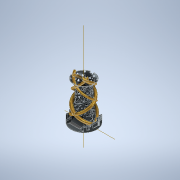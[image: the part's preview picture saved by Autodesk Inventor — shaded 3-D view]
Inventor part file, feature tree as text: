
AUTODESK INVENTOR PART (.ipt)
format: ipt  version: 2022 (Build 260153000, 153)  size: 7,433,728 bytes
history: native  units: mm
features: sketch x27, extrude x26, helix x5, plane x4, fillet x3, revolve x2, pattern_circular x2, chamfer x2
ambient origin geometry x8: Origin, YZ Plane, XZ Plane, XY Plane, X Axis, Y Axis, Z Axis, Center Point
bodies: Solid1 (feature_tree)
feature tree (71):
  revolve  "Revolution1"  [1 undecoded]
  plane  "Work Plane1"
  extrude  "Extrusion4"  Depth=20.0mm
  extrude  "Extrusion2"  Depth=19.0mm
  pattern_circular  "Circular Pattern2"  Count=9  [1 undecoded]
  plane  "Work Plane3"
  extrude  "Extrusion3"  Depth=10.0mm
  pattern_circular  "Circular Pattern3"  Count=7  [1 undecoded]
  helix  "Coil1"  [1 undecoded]
  helix  "Coil2"  [1 undecoded]
  helix  "Coil3"  [1 undecoded]
  helix  "Coil4"  [1 undecoded]
  helix  "Coil5"  [1 undecoded]
  extrude  "Extrusion5"  Depth=20.0mm
  revolve  "Revolution2"  [1 undecoded]
  extrude  "Extrusion6"  Depth=30.0mm
  extrude  "Extrusion15"  Depth=15.0mm
  extrude  "Extrusion16"  Depth=30.0mm
  extrude  "Extrusion17"  Depth=13.0mm
  extrude  "Extrusion18"  Depth=39.0mm
  extrude  "Extrusion19"  Depth=11.0mm
  extrude  "Extrusion20"  Depth=10.0mm
  extrude  "Extrusion21"  Depth=11.0mm
  extrude  "Extrusion22"  Depth=9.0mm
  extrude  "Extrusion23"  Depth=3.0mm TaperAngle=0.0deg
  extrude  "Extrusion25"  Depth=54.0mm TaperAngle=0.0deg
  extrude  "Extrusion26"  Depth=35.0mm
  extrude  "Extrusion27"  Depth=30.0mm
  extrude  "Extrusion28"  Depth=35.0mm
  extrude  "Extrusion29"  Depth=35.0mm
  extrude  "Extrusion30"  Depth=5.0mm
  extrude  "Extrusion31"  Depth=10.0mm TaperAngle=0.0deg
  plane  "Work Plane4"
  extrude  "Extrusion32"  Depth=5.0mm TaperAngle=0.0deg
  extrude  "Extrusion33"  Depth=10.0mm TaperAngle=0.0deg
  chamfer  "Chamfer2"  Distance=15.0mm
  chamfer  "Chamfer3"  Distance=0.2mm
  fillet  "Fillet5"  Radius=5.0mm
  fillet  "Fillet6"  Radius=10.0mm
  extrude  "Extrusion34"  Depth=15.0mm TaperAngle=0.0deg
  fillet  "Fillet16"  Radius=3.0mm
  extrude  "Extrusion35"  Depth=1.0mm TaperAngle=0.0deg
  extrude  "Extrusion36"  Depth=10.0mm TaperAngle=0.0deg
  sketch  "Sketch1"  dims[d11=50.0mm d12=40.0mm]
  sketch  "Sketch3"  dims[d13=20.0mm d14=20.0mm]
  plane  "Work Plane2"
  sketch  "Sketch4"  dims[d15=23.0mm d16=19.0mm d17=90.0mm]
  sketch  "Sketch5"  dims[d18=32.0mm d19=10.0mm]
  sketch  "Sketch7"  dims[d20=151.0mm]
  sketch  "Sketch8"  dims[d26=2.0mm]
  sketch  "Sketch9"  dims[d27=2.0mm]
  sketch  "Sketch10"  dims[d28=2.0mm]
  sketch  "Sketch11"  dims[d29=2.0mm]
  sketch  "Sketch13"  dims[d30=2.0mm]
  sketch  "Sketch16"  dims[d31=90.0deg d32=70.0mm d38=77.75mm d39=0.0mm d40=40.0mm d41=360.0deg d43=70.0mm d44=77.75mm d45=0.0mm d46=40.0mm d47=360.0deg]
  sketch  "Sketch17"  dims[d49=20.0mm d50=20.0mm]
  sketch  "Sketch20"  dims[d51=20.0mm d52=20.0mm]
  sketch  "Sketch21"  dims[d53=40.0mm d54=30.0mm]
  sketch  "Sketch22"  dims[d55=30.0mm d56=15.0mm]
  sketch  "Sketch26"  dims[d57=15.0mm d58=30.0mm]
  sketch  "Sketch27"  dims[d59=77.75mm d60=0.0mm]
  sketch  "Sketch28"  dims[d63=70.0mm d64=100.0mm d65=10.0mm d66=-0.567232mm d67=90.0deg d68=90.0deg d69=90.0deg d70=90.0deg d71=13.0mm]
  sketch  "Sketch30"  dims[d72=10.0mm d73=39.0mm]
  sketch  "Sketch31"  dims[d74=140.0mm d75=160.0mm d76=10.0mm d77=-0.645772mm d78=90.0deg d79=90.0deg d80=90.0deg d81=90.0deg d82=11.0mm]
  sketch  "Sketch33"  dims[d83=39.0mm d84=10.0mm]
  sketch  "Sketch35"  dims[d85=135.0mm d86=160.0mm d87=10.0mm d88=-0.645772mm d89=90.0deg d90=90.0deg d91=90.0deg d92=90.0deg d93=11.0mm]
  sketch  "Sketch37"  dims[d94=170.0mm d95=160.0mm d96=10.0mm d97=-0.645772mm d98=90.0deg d99=90.0deg d100=90.0deg d101=90.0deg d102=9.0mm]
  sketch  "Sketch41"  dims[d103=170.0mm d104=160.0mm d105=10.0mm d106=-0.645772mm d107=90.0deg d108=90.0deg d109=90.0deg d110=90.0deg d125=3.0mm d126=0.0mm]
  sketch  "Sketch43"  dims[d130=270.0deg d133=54.0mm d134=0.0mm]
  sketch  "Sketch44"  dims[d141=35.0mm d165=35.0mm]
  sketch  "Sketch45"  dims[d166=30.0mm d167=30.0mm d168=30.0mm d169=30.0mm d170=35.0mm d172=35.0mm d186=5.0mm d187=10.0mm d188=0.0mm d190=5.0mm d191=0.0mm d192=10.0mm d193=0.0mm d194=15.0mm d195=0.0mm d196=0.2mm d197=0.0mm d198=5.0mm d199=0.0mm d200=10.0mm d201=0.0mm d202=15.0mm d203=0.0mm d204=3.0mm d205=0.0mm d210=1.0mm d211=0.0mm d213=10.0mm d214=0.0mm d218=30.0mm d219=23.5mm d220=5.75mm d221=5.75mm d222=5.75mm d223=14.0mm d224=0.0mm d225=22.5mm d226=6.25mm d227=6.25mm d228=6.25mm d229=14.0mm d230=0.0mm d235=14.0mm d236=0.0mm d241=10.0mm d242=0.0mm d245=17.5mm d251=10.0mm d252=0.0mm d254=21.0mm d258=24.0mm d259=0.0mm d263=25.0mm d266=5.0mm d267=5.0mm d268=12.0mm d269=0.0mm d270=11.0mm d271=2.0mm d272=45.0deg d273=12.0mm d274=2.0mm d275=45.0deg d276=35.0mm d278=5.0mm d279=5.0mm d280=5.0mm d282=2.0mm d283=1.0mm d292=20.0mm d293=0.0mm d295=2.0mm d299=25.0mm d300=52.0mm d301=54.0mm d302=0.0mm d303=25.0mm d304=5.0mm d305=5.0mm d306=5.0mm d307=5.0mm d308=26.0mm d309=3.0mm d310=2.0mm d311=2.484774mm d312=17.5mm d313=21.0mm d314=0.0mm d315=60.0mm d316=200.0mm d317=0.0mm d132=0.0mm d135=0.0mm]
note: 9 required parameter values undecoded (feature->parameter linkage not recoverable at this tier; creation-order binding heuristic only, values carry confidence <= 0.55)